# Revit family: WashBasin-TriangleBowl-47cm-Vitra-PluralSeries-7812
name_source: partatom
category: Plumbing Fixtures
revit_build: Autodesk Revit 2017 (Build: 20160225_1515(x64)
units: mm (PartAtom-declared; Revit-internal decimal feet)

## family parameters
Cut with Voids When Loaded = No
Host = Face
OmniClass Number = 23.45.05.14.14
OmniClass Title = Sinks/Lavatories
Part Type = Normal
Room Calculation Point = No
Round Connector Dimension = Use Diameter
Shared = Yes

## types (13) — shared parameters
BIMobject category = Sanitary - Basins
Brand = VitrA
CW Connection = No
Default Elevation = 850 mm
Description = VitrA Plural Triangle Bowl - 47cm
Design country = Turkey
HW Connection = No
IFC Classification = Sanitary Terminal
Main Material = Ceramic
Manufacturer = Vitra
Manufacturer name = VitrA
Masterformat 2014 Code = 22 41 16
Masterformat 2014 Description = Residential Lavatories and Sinks
Mounting type = Countertop
NBS Referans Code = 35-65-70-94
NBS Referans Description = Wash Basin Systems
Nominal Depth (mm) = 402 mm
Nominal Height (mm) = 130 mm
Nominal Width (mm) = 473 mm
OmniClass Code = 23.45.05.14.14
OmniClass Description = Sinks/Lavatories
Primary Material = <By Category>
Product certification = https://www.vitraglobal.com
Product family = Countertop WashBasin
Product group = Plural
UNSPSC Code = 301815
URL = https://www.vitraglobal.com
Uniclass 1.4 Code = L7212
Uniclass 1.4 Description = Washbasins
Uniclass 2.0 Code = SS-35-65-70-94
Uniclass 2.0 Description = Sanitary Dispensing And Disposal Units
Uniclass 2015 Code = Pr_40_20_96_81
Uniclass 2015 Name = Wash basins, Sinks and troughs
Uniformat II Code = D2010
Uniformat II Description = Plumbing Fixtures
Vent Connection = No
Warranty Period (Year) = 10 Years
Waste Connection = Yes
Weight Net (kg) = 6.7
Youtube = https://www.youtube.com

## per-type parameters (varying)
| type | Article No. (default) | Color | Model | Product SKU | Product data url | Product url | Secondary Material | Technical description |
| WashBasin_Vitra_Plural_(MattTerraRossa)_7812B477-0016 | 7812B477-0016 | Matt Terra Rossa | 7812B477-0016 | 7812B477-0016 | https://www.vitraglobal.com |  | Matt Terra Rossa | https://www.vitraglobal.com |
| WashBasin_Vitra_Plural_(MattMossGreen)_7812B475-0016 | 7812B475-0016 | Matt Moss Green | 7812B475-0016 | 7812B475-0016 | https://www.vitraglobal.com |  | Matt Moss Green | https://www.vitraglobal.com |
| WashBasin_Vitra_Plural_(MattClayBeige)_7812B474-0016 | 7812B474-0016 | Matt Clay Beige | 7812B474-0016 | 7812B474-0016 | https://www.vitraglobal.com |  | Matt Clay Beige | https://www.vitraglobal.com |
| WashBasin_Vitra_Plural_(MatteBlack)_7812B483-0016 | 7812B483-0016 | Matte Black | 7812B483-0016 | 7812B483-0016 | https://www.vitraglobal.com |  | MatteBlack | https://www.vitraglobal.com |
| WashBasin_Vitra_Plural_(MatteMink)_7812B450-0016 | 7812B450-0016 | Matte Mink | 7812B450-0016 | 7812B450-0016 | https://www.vitraglobal.com |  | MatteMink | https://www.vitraglobal.com |
| WashBasin_Vitra_Plural_(MatteBeige)_7812B420-0016 | 7812B420-0016 | Matte Beige | 7812B420-0016 | 7812B420-0016 | https://www.vitraglobal.com |  | MatteBeige | https://www.vitraglobal.com |
| WashBasin_Vitra_Plural_(MatteWhite)_7812B401-0016 | 7812B401-0016 | Matte White | 7812B401-0016 | 7812B401-0016 | https://www.vitraglobal.com |  | MatteWhite | https://www.vitraglobal.com |
| WashBasin_Vitra_Plural_(White)_7812B403-0016 | 7812B403-0016 | White | 7812B403-0016 | 7812B403-0016 | https://www.bimobject.com | https://www.vitraglobal.com | White | https://www.vitraglobal.com |
| WashBasin_Vitra_Plural_(White)_7812B403H0016 | 7812B403H0016 | White | 7812B403H0016 | 7812B403H0016 | https://www.bimobject.com | https://www.vitra-india.com | White | https://www.vitra-india.com |
| WashBasin_Vitra_Plural_(MatteWhite)_7812B401H0016 | 7812B401H0016 | Matte White | 7812B401H0016 | 7812B401H0016 |  | https://www.vitra-india.com | MatteWhite | https://www.vitra-india.com |
| WashBasin_Vitra_Plural_(MatteBeige)_7812B420H0016 | 7812B420H0016 | Matte Beige | 7812B420H0016 | 7812B420H0016 |  | https://www.vitra-india.com | MatteBeige | https://www.vitra-india.com |
| WashBasin_Vitra_Plural_(MatteMink)_7812B450H0016 | 7812B450H0016 | Matte Mink | 7812B450H0016 | 7812B450H0016 |  | https://www.vitra-india.com | MatteMink | https://www.vitra-india.com |
| WashBasin_Vitra_Plural_(MatteBlack)_7812B483H0016 | 7812B483H0016 | Matte Black | 7812B483H0016 | 7812B483H0016 |  | https://www.vitra-india.com | MatteBlack | https://www.vitra-india.com |

## geometry (parser evidence)
native form markers: Sweep x2
no freeform markers — native parametric forms only
